# Revit family: WashBasin-CounterTop-Vitra_GeoSeries_7425B003-0012
name_source: partatom
category: Plumbing Fixtures
revit_build: Autodesk Revit 2017 (Build: 20160225_1515(x64)
units: mm (PartAtom-declared; Revit-internal decimal feet)

## family parameters
Cut with Voids When Loaded = No
Host = Face
OmniClass Number = 23.45.05.14.14
OmniClass Title = Sinks/Lavatories
Part Type = Normal
Room Calculation Point = No
Round Connector Dimension = Use Diameter
Shared = Yes

## types (2) — shared parameters
BIMobject category = Sanitary - Basins
CW Connection = No
Color = White
Default Elevation = 800 mm  [stored 2.62467 ft]
Description = VitrA Geo Soft-Square Countertop Bowl
Design country = Turkey
HW Connection = No
IFC Classification = Sanitary Terminal
Main Material = Ceramic
Manufacturer = Vitra
Manufacturer name = Vitra
Masterformat 2014 Code = 22 41 16
Masterformat 2014 Description = Residential Lavatories and Sinks
MountingType = Counter Top
NBS Referans Code = 35-65-70-94
NBS Referans Description = Wash Basin Systems
Nominal Depth = 395 mm  [stored 1.29593 ft]
NominalHeight = 170 mm  [stored 0.557743 ft]
NominalWidth = 595 mm  [stored 1.9521 ft]
OmniClass Code = 23.45.05.14.14
OmniClass Description = Sinks/Lavatories
Product certification = https://vitraglobal.com
Product data url = https://www.vitra.co.uk
Product family = Counter Top Washbasins
Product group = Geo
Secondary Material = Vitra-Ceramic-White
Technical description = https://www.vitra.co.uk
UNSPSC Code = 301815
URL = https://vitraglobal.com
Uniclass 1.4 Code = L7212
Uniclass 1.4 Description = Washbasins
Uniclass 2.0 Code = SS-35-65-70-94
Uniclass 2.0 Description = Sanitary Dispensing And Disposal Units
Uniclass 2015 Code = Pr_40_20_96_81
Uniclass 2015 Name = Wash basins, Sinks and troughs
Uniformat II Code = D2010
Uniformat II Description = Plumbing Fixtures
Vent Connection = No
Warranty Period (Year) = 10 Years
Waste Connection = Yes
Weight Net (kg) = 14,331
Youtube = https://www.youtube.com
zero-valued in all types: Cost

## per-type parameters (varying)
| type | Article No. (default) | Model | Product SKU |
| WashBasin(CounterTop)-Vitra_GeoSeries_7425B003-0012 | 7425B003-0012 | 7425B003-0012 | 7425B003-0012 |
| WashBasin(CounterTop)-Vitra_GeoSeries_7425B003-0016 | 7425B003-0016 | 7425B003-0016 | 7425B003-0016 |

note: [stored X ft] marks values corroborated as IEEE doubles in the binary element streams (Revit-internal decimal feet)

## geometry (parser evidence)
native form markers: Sweep x3
no freeform markers — native parametric forms only
